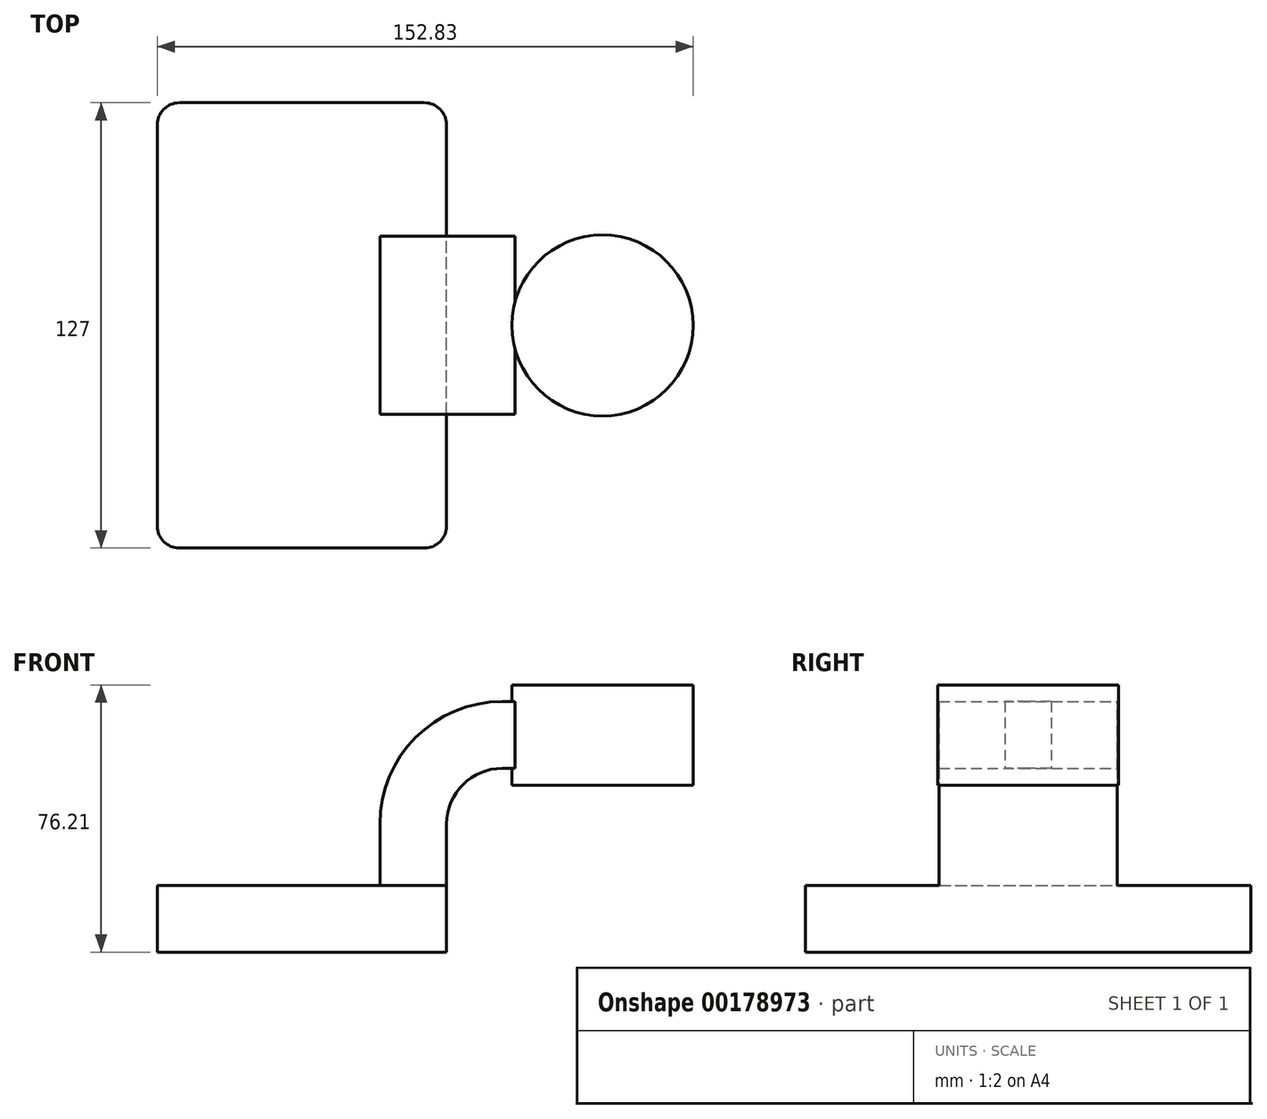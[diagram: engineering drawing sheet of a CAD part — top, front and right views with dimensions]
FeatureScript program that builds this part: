
annotation { "Feature Type Name" : "Feature", "Feature Type Description" : "" }
export const myFeature = defineFeature(function(context is Context, id is Id, definition is map)
    precondition{}
    {
        {
            var Q0;
            Q0=qCreatedBy(makeId("Front.planeOp"),FACE);
            var sketch = newSketch(context, id + "F0", { "sketchPlane" : qUnion([Q0])});
            skLineSegment(sketch, "E0.bottom", {"start": v(-41.28, 9.52) * mm, "end": v(41.28, 9.53) * mm});
            skLineSegment(sketch, "E0.top", {"start": v(-41.28, -9.53) * mm, "end": v(41.28, -9.53) * mm});
            skLineSegment(sketch, "E0.left", {"start": v(-41.28, 9.52) * mm, "end": v(-41.28, -9.53) * mm});
            skLineSegment(sketch, "E0.right", {"start": v(41.28, 9.53) * mm, "end": v(41.28, -9.52) * mm});
            skPoint(sketch, "E0.middle", {"position": v(0, 0) * mm});
            skLineSegment(sketch, "E1.bottom", {"start": v(60.76, 38.1) * mm, "end": v(111.56, 38.1) * mm});
            skLineSegment(sketch, "E1.top", {"start": v(60.76, 66.68) * mm, "end": v(111.56, 66.68) * mm});
            skLineSegment(sketch, "E1.left", {"start": v(60.76, 38.1) * mm, "end": v(60.76, 66.67) * mm});
            skLineSegment(sketch, "E1.right", {"start": v(111.56, 38.1) * mm, "end": v(111.56, 66.67) * mm});
            skPoint(sketch, "E1.middle", {"position": v(86.16, 52.39) * mm});
            skLineSegment(sketch, "E2", {"start": v(41.27, 9.53) * mm, "end": v(41.27, 27) * mm});
            skArc(sketch, "E3", {"start": v(41.27, 27) * mm, "mid": v(45.92, 38.23) * mm, "end": v(57.15, 42.88) * mm});
            skLineSegment(sketch, "E4", {"start": v(57.15, 42.88) * mm, "end": v(85.72, 42.88) * mm});
            skLineSegment(sketch, "E5.0", {"start": v(57.15, 61.93) * mm, "end": v(85.72, 61.93) * mm});
            skArc(sketch, "E5.1", {"start": v(22.22, 27) * mm, "mid": v(32.45, 51.7) * mm, "end": v(57.15, 61.93) * mm});
            skLineSegment(sketch, "E5.2", {"start": v(22.22, 9.53) * mm, "end": v(22.22, 27) * mm});
            skLineSegment(sketch, "E6", {"start": v(85.72, 38.1) * mm, "end": v(85.72, 66.68) * mm});
            skFitSpline(sketch, "E7", {"points": [v(-41.28, 9.52) * mm, v(57.15, 61.93) * mm], "startDerivative": vector(1.16, 100) * mm, "endDerivative": vector(141.17, -1.5) * mm});
            skSolve(sketch);
        }
        {
            var Q0;
            Q0=makeQuery(id+"F0.imprint","IMPRINT",FACE,{"disambiguationData":[TD([[makeQuery(id+"F0.imprint","IMPRINT",EDGE,{"derivedFrom":sQuery(id+"F0.wireOp",EDGE,"E0.top")}),1.0]])]});
            extrude(context, id + "F1", {"entities" : qUnion([Q0]), "endBound" : BoundingType.SYMMETRIC, "depth" : 127 * mm});
        }
        {
            var Q0;
            {var subQ2=sQuery(id+"F0.wireOp",EDGE,"E2");Q0=makeQuery(id+"F0.imprint","IMPRINT",FACE,{"disambiguationData":[TD([[makeQuery(id+"F0.imprint","IMPRINT",EDGE,{"derivedFrom":subQ2}),1.0]])]});}
            extrude(context, id + "F2", {"entities" : qUnion([Q0]), "operationType" : NewBodyOperationType.ADD, "endBound" : BoundingType.SYMMETRIC, "depth" : 50.8 * mm});
        }
        {
            var Q0;
            Q0=makeQuery(id+"F0.imprint","IMPRINT",FACE,{"disambiguationData":[TD([[makeQuery(id+"F0.imprint","IMPRINT",EDGE,{"derivedFrom":sQuery(id+"F0.wireOp",EDGE,"E5.1")}),1.0]])]});
            extrude(context, id + "F3", {"entities" : qUnion([Q0]), "operationType" : NewBodyOperationType.ADD, "endBound" : BoundingType.SYMMETRIC, "depth" : 15.88 * mm});
        }
        {
            var Q0;
            {var subQ0=sQuery(id+"F0.wireOp",EDGE,"E1.right");Q0=makeQuery(id+"F0.imprint","IMPRINT",FACE,{"disambiguationData":[TD([[makeQuery(id+"F0.imprint","IMPRINT",EDGE,{"derivedFrom":subQ0}),1.0]])]});}
            var Q1;
            Q1=sQuery(id+"F0.wireOp",EDGE,"E6");
            revolve(context, id + "F4", {"operationType" : NewBodyOperationType.ADD, "entities" : qUnion([Q0]), "axis" : qUnion([Q1]), "revolveType" : RevolveType.FULL});
        }
        {
            var Q0;
            Q0=makeQuery(id+"F1.opExtrude","CAP_EDGE",EDGE,{"disambiguationData":[OSD([sQuery(id+"F0.wireOp",EDGE,"E0.left")])],"isStart":false});
            var Q1;
            Q1=makeQuery(id+"F1.opExtrude","CAP_EDGE",EDGE,{"disambiguationData":[OSD([sQuery(id+"F0.wireOp",EDGE,"E0.right")])],"isStart":false});
            var Q2;
            Q2=makeQuery(id+"F1.opExtrude","CAP_EDGE",EDGE,{"disambiguationData":[OSD([sQuery(id+"F0.wireOp",EDGE,"E0.left")])],"isStart":true});
            var Q3;
            Q3=makeQuery(id+"F1.opExtrude","CAP_EDGE",EDGE,{"disambiguationData":[OSD([sQuery(id+"F0.wireOp",EDGE,"E0.right")])],"isStart":true});
            fillet(context, id + "F5", {"entities" : qUnion([Q0, Q1, Q2, Q3]), "radius" : 6.35 * mm, "tangentPropagation" : true, "allowEdgeOverflow" : false});
        }
    });
